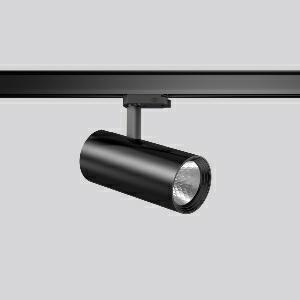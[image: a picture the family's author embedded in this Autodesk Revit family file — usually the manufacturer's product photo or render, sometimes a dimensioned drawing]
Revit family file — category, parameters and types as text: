
# Revit family: deecos_s_mini_742205_003_3_92c5
name_source: partatom
category: Lighting Fixtures
units: mm (PartAtom-declared; Revit-internal decimal feet)

## family parameters
Cut with Voids When Loaded = No
Host = Face
Light Source = No
Part Type = Normal
Room Calculation Point = No
Round Connector Dimension = Use Diameter
Shared = No

## types (1)
- DEECOS S mini (1 x LED Modul 935, 3800 lm, 3500)
    Apparent Load = 29 VA
    Approval mark = CE
    CIE Flux Codes = 95 99 100 100 100
    Color Rendering = 92
    Color Temperature = 3500
    Default Elevation = 1800 mm
    Description = Series: DEECOS S mini
LED surface-mounted projector in modern design with no visible cooling ribs. Housing: die-cast aluminium, powder-coated. Rotation range: 356°. Swivel range: 90°. Black plastic ring and recessed LED to prevent glare from the side. Optical assembly with reflector made of MIRO-Silver with 98% total light reflection for outstanding efficiency - can be changed without tools. Best colour rendering index Ra>90. With multi adaptor for 3-circuit tracks 230 V. Suitable for Track on ceiling, Wall track. High quality converter without flickering and stroboscopic effect. The following accessories can be mounted without use of tools: interchangeable lenses, decorative glasses, honeycomb louvre, clear and frosted diffusers, white interchangeable plastic ring. 
Colour: deep black, matt (RAL 9005)
Diameter: 87 mm
Height: 214 mm
Lamp: LED
Socket: without socket
Colour temperature: 3500K
Colour rendering index (CRI): 92
System power: 29 W
Rated luminous flux: 3800 lm
Luminous efficiency: 131 lm/W
Control gear: Regulated power supply
Protection class: I
Type of protection: IP 20
    Height = 214 mm
    Lamp = 1 x LED Modul 935
    Lamp Light Flux = 3800 lm
    Lamp count = 1
    Length = 87 mm
    Lifetime = 50000 h
    Luminous efficacy = 131 lm/W
    Manufacturer = RZB
    ModVariant = No
    Model = 742205.003.3
    Mounting Place = Ceiling
    Mounting Type = Rail mounted
    Number of Poles = 1
    OnlyDefault = Yes
    Power Factor = 1
    Product Name = DEECOS S mini
    Product group = Track mounted projectors
    ProductGroupID = 301
    Protection Class = Protection class I
    Protection Degree = IP 20
    RLX_Detail_Level = 1
    RLX_Emergency_Light_Flux = 0 lm
    RLX_Emergency_Type = 0
    RLX_Emergency_Type_DB = No
    RlxData = <blob elided: 39057 chars, md5=782a72b4>
    Socket = socket
    Standby Power = 0 W
    System Light Flux = 3800 lm
    System Power = 29 W
    Type Comments = Product without accessories
    Type Image = 741926.003.jpg
    URL = http://relux.com
    VarID = ---
    Voltage = 230 V
    Voltage Range = 220-240 V
    Weight = 0.00 kg
    Width = 0 mm  [stored 0 ft]

note: [stored X ft] marks values corroborated as IEEE doubles in the binary element streams (Revit-internal decimal feet)

## geometry (parser evidence)
native form markers: Blend x4, Sweep x11
no freeform markers — native parametric forms only
